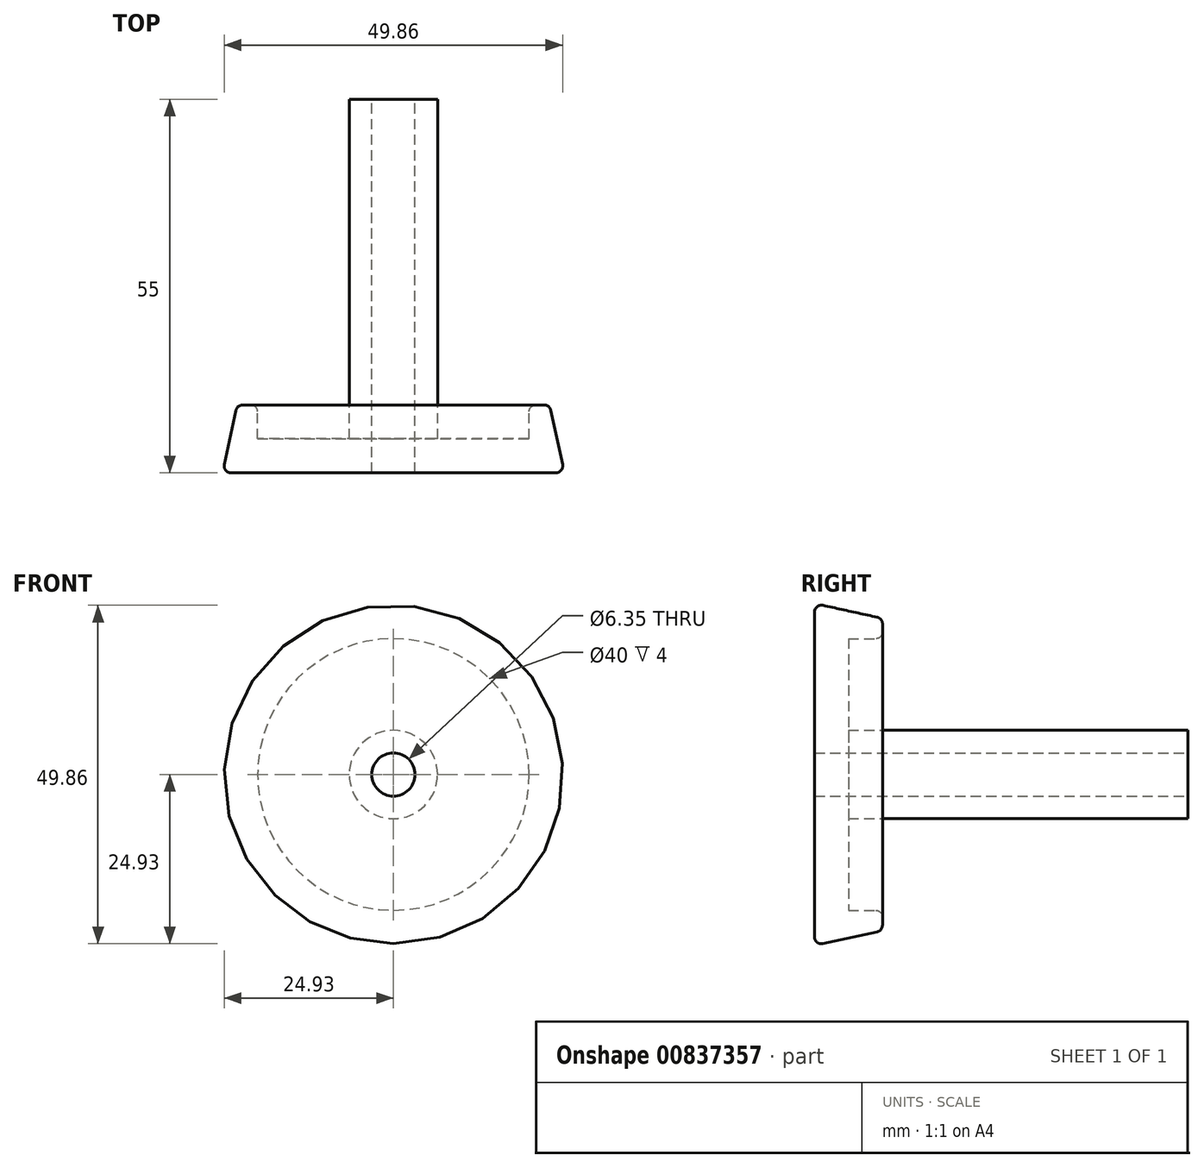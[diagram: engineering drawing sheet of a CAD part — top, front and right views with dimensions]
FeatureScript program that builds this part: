
annotation { "Feature Type Name" : "Feature", "Feature Type Description" : "" }
export const myFeature = defineFeature(function(context is Context, id is Id, definition is map)
    precondition{}
    {
        {
            var Q0;
            Q0=qCreatedBy(makeId("Top.planeOp"),FACE);
            var sketch = newSketch(context, id + "F0", { "sketchPlane" : qUnion([Q0])});
            skLineSegment(sketch, "E0", {"start": v(-3.18, 0) * mm, "end": v(-3.18, 55) * mm});
            skLineSegment(sketch, "E1", {"start": v(-3.18, 55) * mm, "end": v(-6.5, 55) * mm});
            skLineSegment(sketch, "E2", {"start": v(-6.5, 55) * mm, "end": v(-6.5, 5) * mm});
            skLineSegment(sketch, "E3", {"start": v(-6.5, 5) * mm, "end": v(-20, 5) * mm});
            skLineSegment(sketch, "E4", {"start": v(-20, 5) * mm, "end": v(-20, 10) * mm});
            skLineSegment(sketch, "E5", {"start": v(-20, 10) * mm, "end": v(-23, 10) * mm});
            skLineSegment(sketch, "E6", {"start": v(-23, 10) * mm, "end": v(-25.18, 0) * mm});
            skLineSegment(sketch, "E7", {"start": v(-25.18, 0) * mm, "end": v(-3.18, 0) * mm});
            skLineSegment(sketch, "E8", {"start": v(0, 61.87) * mm, "end": v(0, 0) * mm, "construction": true});
            skSolve(sketch);
        }
        {
            var Q0;
            Q0=makeQuery(id+"F0.imprint","IMPRINT",FACE,{"disambiguationData":[TD([[makeQuery(id+"F0.imprint","IMPRINT",EDGE,{"derivedFrom":sQuery(id+"F0.wireOp",EDGE,"E0")}),1.0]])]});
            var Q1;
            Q1=sQuery(id+"F0.wireOp",EDGE,"E8");
            revolve(context, id + "F1", {"surfaceOperationType" : NewSurfaceOperationType.NEW, "entities" : qUnion([Q0]), "axis" : qUnion([Q1]), "revolveType" : RevolveType.FULL});
        }
        {
            var Q0;
            Q0=makeQuery(id+"F1.opRevolve","SWEPT_EDGE",EDGE,{"disambiguationData":[OSD([sQuery(id+"F0.wireOp",EDGE,"E6"),sQuery(id+"F0.wireOp",EDGE,"E7")])]});
            var Q1;
            Q1=makeQuery(id+"F1.opRevolve","SWEPT_EDGE",EDGE,{"disambiguationData":[OSD([sQuery(id+"F0.wireOp",EDGE,"E5"),sQuery(id+"F0.wireOp",EDGE,"E6")])]});
            var Q2;
            Q2=makeQuery(id+"F1.opRevolve","SWEPT_EDGE",EDGE,{"disambiguationData":[OSD([sQuery(id+"F0.wireOp",EDGE,"E4"),sQuery(id+"F0.wireOp",EDGE,"E5")])]});
            fillet(context, id + "F2", {"entities" : qUnion([Q0, Q1, Q2]), "radius" : 1 * mm, "tangentPropagation" : true, "allowEdgeOverflow" : false});
        }
    });
